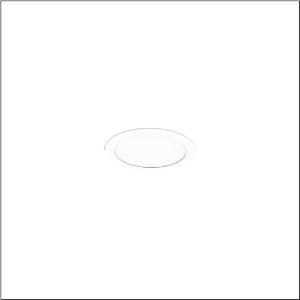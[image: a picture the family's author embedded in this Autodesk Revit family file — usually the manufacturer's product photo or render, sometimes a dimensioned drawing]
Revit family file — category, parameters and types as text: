
# Revit family: lunis_21_m_51db16mc91c
name_source: partatom
category: Lighting Fixtures
units: mm (PartAtom-declared; Revit-internal decimal feet)

## family parameters
Cut with Voids When Loaded = No
Host = Face
Light Source = No
Part Type = Normal
Room Calculation Point = No
Round Connector Dimension = Use Diameter
Shared = No

## types (1)
- --- (1 x LED, 3280 lm, 25.5 W, 6500K)
    Apparent Load = 26 VA
    CIE Flux Codes = 50 80 96 100 100
    Color Rendering = 80
    Color Temperature = 6500K
    Default Elevation = 1800 mm
    Description = Lunis 21,  M, downlight, light control with lens, of PMMA, optical cover: cover panel, of PC, opal, light emission: direct distribution, LED rated luminous flux: 1.490lm, light colour: 830/840/865, with terminal, 3-pole, mains connection: 220..240V, AC/DC, 0/50..60Hz, housing, round, of diecast aluminium, traffic white (RAL 9016), diameter: 115mm, clamping range: 1..40mm, protection rating (complete): IP20, protection rating (on room side): IP54, insulation class (complete): insulation class II (safety insulation), certification: CE, impact resistance: IK03, packaging unit: 1 piece
    Height = 0 mm  [stored 0 ft]
    Lamp = 1 x LED
    Lamp Light Flux = 3280 lm
    Lamp Power = 25.5 W
    Lamp count = 1
    Length = 115 mm
    Luminous efficacy = 129 lm/W
    Manufacturer = Siteco
    ModVariant = No
    Model = 51DB16MC91C
    Mounting Place = Ceiling
    Mounting Type = Recessed
    Number of Poles = 1
    OnlyDefault = Yes
    Power Factor = 1
    Product Name = Lunis 21 M
    Product group = downlight
    ProductGroupID = 400
    Protection Class = Protection class II
    Protection Degree = IP 20
    RLX_Detail_Level = 1
    RLX_Emergency_Light_Flux = 0 lm
    RLX_Emergency_Type = 0
    RLX_Emergency_Type_DB = No
    RlxData = <blob elided: 13509 chars, md5=ea2bdf7f>
    Socket = socket
    Standby Power = 0 W
    System Light Flux = 3280 lm
    System Power = 26 W
    Type Comments = individual setting: colour temperature 6500K, luminous flux: 100 % | (ON | ON | OFF | OFF) | 700 mA
    Type Image = l_1290848.jpg
    URL = http://relux.com
    VarID = @adj_013176
    Voltage = 0 V
    Weight = 0.00 kg
    Width = 0 mm  [stored 0 ft]

note: [stored X ft] marks values corroborated as IEEE doubles in the binary element streams (Revit-internal decimal feet)

## geometry (parser evidence)
native form markers: Sweep x10
no freeform markers — native parametric forms only
